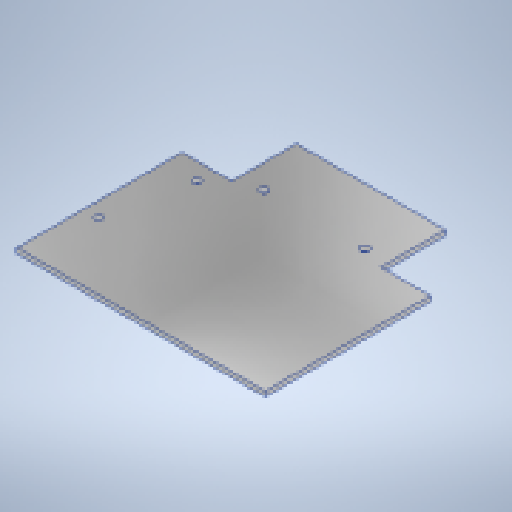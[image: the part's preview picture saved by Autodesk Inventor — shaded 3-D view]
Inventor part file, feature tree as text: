
AUTODESK INVENTOR PART (.ipt)
format: ipt  version: 2023 (Build 270158000, 158)  size: 215,040 bytes
history: native  units: mm
features: extrude x10, sketch x10, projected_geometry x3, other x2, reference x1
ambient origin geometry x8: Origin, YZ Plane, XZ Plane, XY Plane, X Axis, Y Axis, Z Axis, Center Point
bodies: Solid1 (feature_tree)
feature tree (26):
  extrude  "Extrusion1"  Depth=100.0mm
  extrude  "Extrusion2"  Depth=20.0mm
  extrude  "Wyciągnięcie proste3"  Depth=10.0mm
  extrude  "Wyciągnięcie proste4"  Depth=20.0mm
  extrude  "Wyciągnięcie proste5"  Depth=2.0mm TaperAngle=0.0deg
  extrude  "Wyciągnięcie proste6"  Depth=10.0mm
  extrude  "Wyciągnięcie proste7"  Depth=2.0mm TaperAngle=0.0deg
  sketch  "Szkic8"
  extrude  "Wyciągnięcie proste8"  TaperAngle=0.0deg  [1 undecoded]
  extrude  "Wyciągnięcie proste9"  Depth=10.0mm TaperAngle=0.0deg
  extrude  "Wyciągnięcie proste10"  TaperAngle=0.0deg  [1 undecoded]
  sketch  "Sketch1"  dims[d0=100.0mm d1=100.0mm]
  sketch  "Sketch2"  dims[d2=5.0mm d3=20.0mm d4=31.0mm d5=20.0mm d6=2.0mm d7=0.0mm d8=5.0mm d9=2.0mm d10=0.0mm d11=0.0mm d12=0.0mm d13=10.0mm d14=0.0mm d15=0.0mm d16=0.0mm d17=2.5mm d18=0.0mm d19=0.0mm d20=0.0mm d21=25.6mm d22=28.0mm d23=0.0mm d24=0.0mm d25=0.0mm d26=0.0mm d27=0.0mm d28=0.0mm]
  reference  "Reference1"
  sketch  "Szkic3"
  sketch  "Szkic4"
  projected_geometry  "Pętla rzutowana1"
  sketch  "Szkic5"
  sketch  "Szkic6"
  projected_geometry  "Pętla rzutowana2"
  sketch  "Szkic7"
  projected_geometry  "Pętla rzutowana3"
  sketch  "Szkic9"
  sketch  "Szkic10"
  other  "Assembly2"
  other  "dach]:1"
note: 2 required parameter values undecoded (feature->parameter linkage not recoverable at this tier; creation-order binding heuristic only, values carry confidence <= 0.55)
